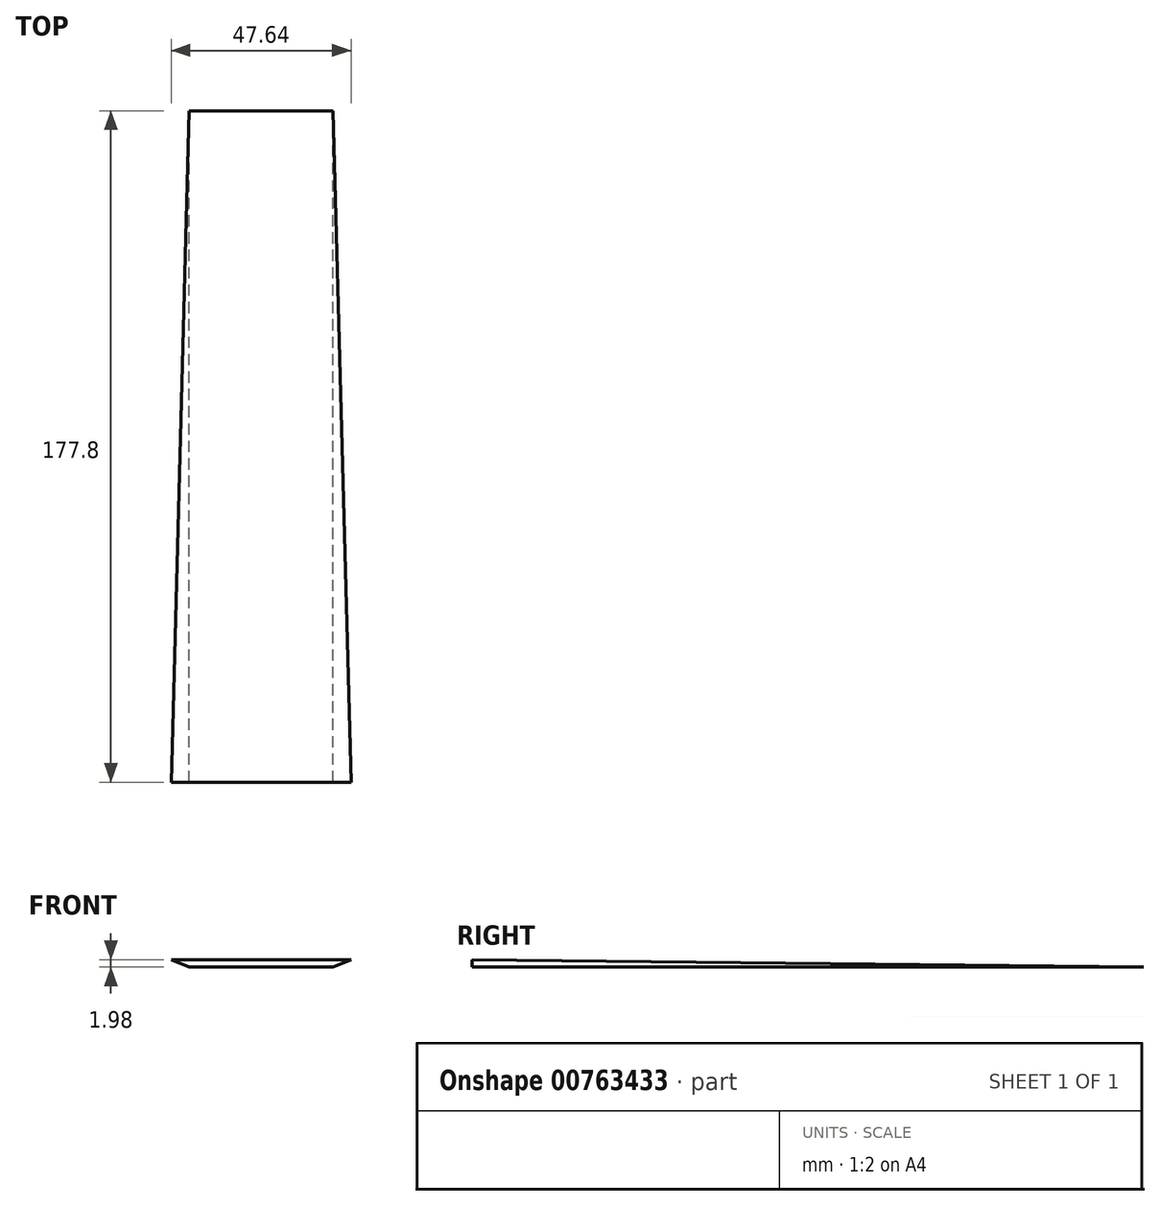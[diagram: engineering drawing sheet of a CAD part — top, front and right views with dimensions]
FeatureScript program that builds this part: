
annotation { "Feature Type Name" : "Feature", "Feature Type Description" : "" }
export const myFeature = defineFeature(function(context is Context, id is Id, definition is map)
    precondition{}
    {
        {
            var Q0;
            Q0=qCreatedBy(makeId("Front.planeOp"),FACE);
            var sketch = newSketch(context, id + "F0", { "sketchPlane" : qUnion([Q0])});
            skLineSegment(sketch, "E0.bottom", {"start": v(0, 0) * mm, "end": v(19.05, 0) * mm});
            skLineSegment(sketch, "E0.left", {"start": v(0, 0) * mm, "end": v(0, 1.98) * mm});
            skLineSegment(sketch, "E1", {"start": v(0, 21.75) * mm, "end": v(0, -18.45) * mm, "construction": true});
            skLineSegment(sketch, "E2", {"start": v(0, 1.98) * mm, "end": v(23.83, 1.98) * mm});
            skLineSegment(sketch, "E3", {"start": v(23.83, 1.98) * mm, "end": v(19.05, 0) * mm});
            skLineSegment(sketch, "E4.MirrorCS", {"start": v(-23.83, 1.98) * mm, "end": v(-19.05, 0) * mm});
            skLineSegment(sketch, "E5.MirrorCS", {"start": v(0, 1.98) * mm, "end": v(-23.83, 1.98) * mm});
            skLineSegment(sketch, "E6.MirrorCS", {"start": v(0, 0) * mm, "end": v(-19.05, 0) * mm});
            skSolve(sketch);
        }
        {
            var Q0;
            Q0=makeQuery(id+"F0.imprint","IMPRINT",FACE,{"disambiguationData":[TD([[makeQuery(id+"F0.imprint","IMPRINT",EDGE,{"derivedFrom":sQuery(id+"F0.wireOp",EDGE,"E0.bottom")}),1.0]])]});
            var Q1;
            Q1=makeQuery(id+"F0.imprint","IMPRINT",FACE,{"disambiguationData":[TD([[makeQuery(id+"F0.imprint","IMPRINT",EDGE,{"derivedFrom":sQuery(id+"F0.wireOp",EDGE,"c3a80ad8-3808-42c9-9b79-f9b212de4d1c0.MirrorCS")}),-1.0]])]});
            var Q2;
            Q2=makeQuery(id+"F0.imprint","IMPRINT",FACE,{"disambiguationData":[TD([[makeQuery(id+"F0.imprint","IMPRINT",EDGE,{"derivedFrom":sQuery(id+"F0.wireOp",EDGE,"E0.left")}),1.0]])]});
            extrude(context, id + "F1", {"entities" : qUnion([Q0, Q1, Q2]), "depth" : 177.8 * mm, "offsetDistance" : 25.4 * mm});
        }
        {
            var Q0;
            Q0=qCreatedBy(makeId("Right.planeOp"),FACE);
            var sketch = newSketch(context, id + "F2", { "sketchPlane" : qUnion([Q0])});
            skLineSegment(sketch, "E7", {"start": v(0, 0) * mm, "end": v(0, 5.33) * mm});
            skLineSegment(sketch, "E8", {"start": v(0, 0) * mm, "end": v(-177.8, 1.98) * mm});
            skLineSegment(sketch, "E9", {"start": v(-177.8, 1.98) * mm, "end": v(-177.8, 1.99) * mm});
            skLineSegment(sketch, "E10", {"start": v(-177.8, 1.99) * mm, "end": v(0, 5.33) * mm});
            skSolve(sketch);
        }
        {
            var Q0;
            Q0 = qSketchRegion(id + "F2", true);
            extrude(context, id + "F3", {"entities" : qUnion([Q0]), "operationType" : NewBodyOperationType.REMOVE, "endBound" : BoundingType.SYMMETRIC, "oppositeDirection" : true, "depth" : 50.8 * mm, "offsetDistance" : 25.4 * mm});
        }
    });
